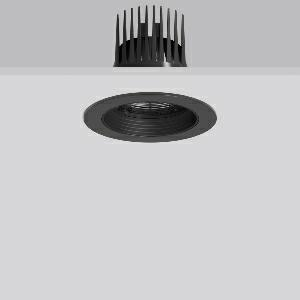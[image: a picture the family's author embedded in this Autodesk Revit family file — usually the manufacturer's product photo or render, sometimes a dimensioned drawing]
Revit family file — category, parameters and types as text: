
# Revit family: heledon_maxi_e_901769_003_76_7a91
name_source: partatom
category: Lighting Fixtures
units: mm (PartAtom-declared; Revit-internal decimal feet)

## family parameters
Cut with Voids When Loaded = No
Host = Face
Light Source = No
Part Type = Normal
Room Calculation Point = No
Round Connector Dimension = Use Diameter
Shared = No

## types (1)
- HELEDON maxi E (1 x LED Modul 930, 3600 lm, 3000)
    Apparent Load = 35 VA
    Approval mark = CE
    CIE Flux Codes = 96 100 100 100 100
    Color Rendering = 90
    Color Temperature = 3000
    Default Elevation = 1800 mm
    Description = Series: HELEDON maxi
Round recessed downlight. Housing: die-cast aluminium, powder-coated. Black plastic ring and recessed LED to prevent glare from the side. Optical assembly with lens made of plastic (polycarbonate) for the best homogeneous light distribution - can be changed without tools. Best colour rendering index Ra>90. Suitable for Recessed ceiling mounting. Installation without tools thanks to spring fastening system. Including separate LED converter with connecting cable 600 mm.High quality converter without flickering and stroboscopic effect. Through-wiring box (5 pole) available as accessory. The following accessories can be mounted without use of tools: interchangeable lenses, decorative glasses, honeycomb louvre, clear and frosted diffusers, white interchangeable plastic ring. 
Colour: deep black, matt (RAL 9005)
Diameter: 162 mm
Height: 3 mm
Cut-out diameter: 152 mm
Recess height: 200 mm
Luminaire: recess height: 135 mm
Lamp: LED
Socket: without socket
Colour temperature: 3000K
Colour rendering index (CRI): 92
System power: 35 W
Rated luminous flux: 3600 lm
Luminous efficiency: 103 lm/W
Control gear: Converter, dimmable, DALI
Protection class: II
Type of protection: IP 20
    Height = 0 mm  [stored 0 ft]
    Lamp = 1 x LED Modul 930
    Lamp Light Flux = 3600 lm
    Lamp count = 1
    Length = 162 mm
    Lifetime = 50000 h
    Luminous efficacy = 103 lm/W
    Manufacturer = RZB
    ModVariant = No
    Model = 901769.003.76
    Mounting Place = Ceiling
    Mounting Type = Recessed
    Number of Poles = 1
    OnlyDefault = Yes
    Power Factor = 1
    Product Name = HELEDON maxi E
    Product group = Recessed downlights
    ProductGroupID = 402
    Protection Class = Protection class II
    Protection Degree = IP 20
    RLX_Detail_Level = 1
    RLX_Emergency_Light_Flux = 0 lm
    RLX_Emergency_Type = 0
    RLX_Emergency_Type_DB = No
    RlxData = <blob elided: 119465 chars, md5=c7369139>
    Socket = socket
    Standby Power = 0 W
    System Light Flux = 3600 lm
    System Power = 35 W
    Type Comments = Product without accessories
    Type Image = 901663.003.jpg
    URL = http://relux.com
    VarID = ---
    Voltage = 230 V
    Voltage Range = 220-240 V
    Weight = 0.00 kg
    Width = 0 mm  [stored 0 ft]

note: [stored X ft] marks values corroborated as IEEE doubles in the binary element streams (Revit-internal decimal feet)

## geometry (parser evidence)
native form markers: Blend x4, Sweep x11
no freeform markers — native parametric forms only
